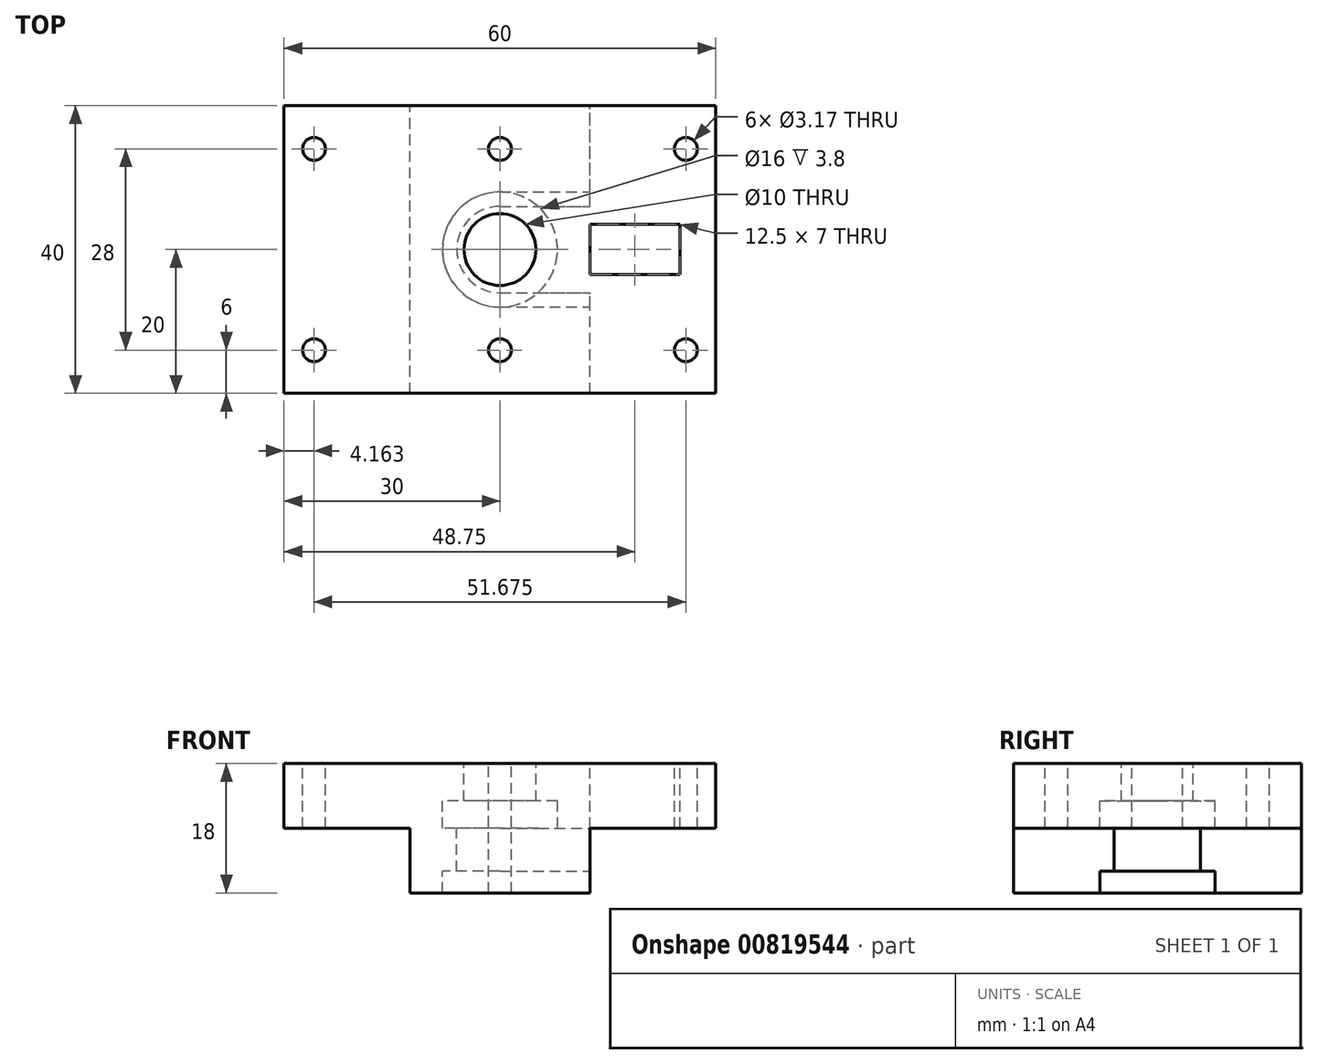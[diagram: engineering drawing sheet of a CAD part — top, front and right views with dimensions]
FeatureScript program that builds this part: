
annotation { "Feature Type Name" : "Feature", "Feature Type Description" : "" }
export const myFeature = defineFeature(function(context is Context, id is Id, definition is map)
    precondition{}
    {
        {
            var Q0;
            Q0=qCreatedBy(makeId("Top.planeOp"),FACE);
            var sketch = newSketch(context, id + "F0", { "sketchPlane" : qUnion([Q0])});
            skLineSegment(sketch, "E0.bottom", {"start": v(30, 20) * mm, "end": v(-30, 20) * mm});
            skLineSegment(sketch, "E0.top", {"start": v(30, -20) * mm, "end": v(-30, -20) * mm});
            skLineSegment(sketch, "E0.left", {"start": v(30, 20) * mm, "end": v(30, -20) * mm});
            skLineSegment(sketch, "E0.right", {"start": v(-30, 20) * mm, "end": v(-30, -20) * mm});
            skPoint(sketch, "E0.middle", {"position": v(0, 0) * mm});
            skLineSegment(sketch, "E1", {"start": v(-30, -20) * mm, "end": v(-30, -43.75) * mm});
            skLineSegment(sketch, "E2", {"start": v(30, -43.75) * mm, "end": v(30, -20) * mm});
            skLineSegment(sketch, "E3.bottom", {"start": v(24.25, -38.25) * mm, "end": v(-24.25, -38.25) * mm});
            skLineSegment(sketch, "E3.top", {"start": v(24.25, -21.75) * mm, "end": v(-24.25, -21.75) * mm});
            skLineSegment(sketch, "E3.left", {"start": v(24.25, -38.25) * mm, "end": v(24.25, -21.75) * mm});
            skLineSegment(sketch, "E3.right", {"start": v(-24.25, -38.25) * mm, "end": v(-24.25, -21.75) * mm});
            skPoint(sketch, "E3.middle", {"position": v(0, -30) * mm});
            skLineSegment(sketch, "E4", {"start": v(-24.25, -21.75) * mm, "end": v(-24.25, -20) * mm});
            skLineSegment(sketch, "E5", {"start": v(24.25, -21.75) * mm, "end": v(24.25, -20) * mm});
            skCircle(sketch, "E6", {"center": v(0, 0) * mm, "radius": 8 * mm});
            skCircle(sketch, "E7", {"center": v(0, -50) * mm, "radius": 6 * mm});
            skArc(sketch, "E8", {"start": v(-8.8, -60.89) * mm, "mid": v(0, -64) * mm, "end": v(8.8, -60.89) * mm});
            skLineSegment(sketch, "E9", {"start": v(-30, -43.75) * mm, "end": v(-8.8, -60.89) * mm});
            skLineSegment(sketch, "E10.MirrorCS", {"start": v(30, -43.75) * mm, "end": v(8.8, -60.89) * mm});
            skPoint(sketch, "E11.orphan", {"position": v(30, -62.25) * mm});
            skPoint(sketch, "E12.orphan", {"position": v(-30, -62.25) * mm});
            skCircle(sketch, "E13.MirrorC", {"center": v(-14, -50) * mm, "radius": 1.65 * mm});
            skCircle(sketch, "E14", {"center": v(0, 0) * mm, "radius": 5 * mm});
            skCircle(sketch, "E15", {"center": v(-25.84, 14) * mm, "radius": 1.59 * mm});
            skCircle(sketch, "E16.MirrorC", {"center": v(25.84, 14) * mm, "radius": 1.59 * mm});
            skCircle(sketch, "E17.MirrorC", {"center": v(25.84, -14) * mm, "radius": 1.59 * mm});
            skCircle(sketch, "E18.MirrorC", {"center": v(-25.84, -14) * mm, "radius": 1.59 * mm});
            skCircle(sketch, "E19.MirrorC", {"center": v(14, -50) * mm, "radius": 1.65 * mm});
            skCircle(sketch, "E20", {"center": v(14, -50) * mm, "radius": 3.85 * mm});
            skCircle(sketch, "E21.MirrorC", {"center": v(-14, -50) * mm, "radius": 3.85 * mm});
            skLineSegment(sketch, "E22.bottom", {"start": v(25, -3.5) * mm, "end": v(12.5, -3.5) * mm});
            skLineSegment(sketch, "E22.top", {"start": v(25, 3.5) * mm, "end": v(12.5, 3.5) * mm});
            skLineSegment(sketch, "E22.left", {"start": v(25, -3.5) * mm, "end": v(25, 3.5) * mm});
            skLineSegment(sketch, "E22.right", {"start": v(12.5, -3.5) * mm, "end": v(12.5, 3.5) * mm});
            skPoint(sketch, "E22.middle", {"position": v(18.75, 0) * mm});
            skCircle(sketch, "E23", {"center": v(0, 14) * mm, "radius": 1.59 * mm});
            skCircle(sketch, "E24.MirrorC", {"center": v(0, -14) * mm, "radius": 1.59 * mm});
            skSolve(sketch);
        }
        {
            var Q0;
            Q0=makeQuery(id+"F0.imprint","IMPRINT",FACE,{"disambiguationData":[TD([[makeQuery(id+"F0.imprint","IMPRINT",EDGE,{"derivedFrom":sQuery(id+"F0.wireOp",EDGE,"E0.bottom")}),1.0]])]});
            extrude(context, id + "F1", {"entities" : qUnion([Q0]), "oppositeDirection" : true, "depth" : 9 * mm, "offsetDistance" : 25 * mm});
        }
        {
            var Q0;
            Q0=makeQuery(id+"F0.imprint","IMPRINT",FACE,{"disambiguationData":[TD([[makeQuery(id+"F0.imprint","IMPRINT",EDGE,{"derivedFrom":sQuery(id+"F0.wireOp",EDGE,"E6")}),1.0]])]});
            var Q1;
            Q1=makeQuery(id+"F1.opExtrude","CAP_FACE",FACE,{"disambiguationData":[OSD([sQuery(id+"F0.wireOp",EDGE,"E0.bottom"),sQuery(id+"F0.wireOp",EDGE,"E0.top"),sQuery(id+"F0.wireOp",EDGE,"E0.left"),sQuery(id+"F0.wireOp",EDGE,"E0.right"),sQuery(id+"F0.wireOp",EDGE,"E1"),sQuery(id+"F0.wireOp",EDGE,"E2"),sQuery(id+"F0.wireOp",EDGE,"E3.bottom"),sQuery(id+"F0.wireOp",EDGE,"E3.left"),sQuery(id+"F0.wireOp",EDGE,"E3.right"),sQuery(id+"F0.wireOp",EDGE,"E4"),sQuery(id+"F0.wireOp",EDGE,"E5"),sQuery(id+"F0.wireOp",EDGE,"E6"),sQuery(id+"F0.wireOp",EDGE,"E7"),sQuery(id+"F0.wireOp",EDGE,"E8"),sQuery(id+"F0.wireOp",EDGE,"E9"),sQuery(id+"F0.wireOp",EDGE,"E10.MirrorCS"),sQuery(id+"F0.wireOp",EDGE,"E13.MirrorC"),sQuery(id+"F0.wireOp",EDGE,"E15"),sQuery(id+"F0.wireOp",EDGE,"E16.MirrorC"),sQuery(id+"F0.wireOp",EDGE,"E17.MirrorC"),sQuery(id+"F0.wireOp",EDGE,"E18.MirrorC"),sQuery(id+"F0.wireOp",EDGE,"E19.MirrorC")])],"isStart":false});
            extrude(context, id + "F2", {"entities" : qUnion([Q0]), "operationType" : NewBodyOperationType.ADD, "endBound" : BoundingType.UP_TO_SURFACE, "oppositeDirection" : true, "depth" : 2.2 * mm, "endBoundEntityFace" : qUnion([Q1]), "hasOffset" : true, "offsetDistance" : 3.8 * mm});
        }
        {
            var Q0;
            Q0=makeQuery(id+"F1.opExtrude","CAP_FACE",FACE,{"disambiguationData":[OSD([sQuery(id+"F0.wireOp",EDGE,"E0.bottom"),sQuery(id+"F0.wireOp",EDGE,"E0.top"),sQuery(id+"F0.wireOp",EDGE,"E0.left"),sQuery(id+"F0.wireOp",EDGE,"E0.right"),sQuery(id+"F0.wireOp",EDGE,"E1"),sQuery(id+"F0.wireOp",EDGE,"E2"),sQuery(id+"F0.wireOp",EDGE,"E3.bottom"),sQuery(id+"F0.wireOp",EDGE,"E3.left"),sQuery(id+"F0.wireOp",EDGE,"E3.right"),sQuery(id+"F0.wireOp",EDGE,"E4"),sQuery(id+"F0.wireOp",EDGE,"E5"),sQuery(id+"F0.wireOp",EDGE,"E6"),sQuery(id+"F0.wireOp",EDGE,"E7"),sQuery(id+"F0.wireOp",EDGE,"E8"),sQuery(id+"F0.wireOp",EDGE,"E9"),sQuery(id+"F0.wireOp",EDGE,"E10.MirrorCS"),sQuery(id+"F0.wireOp",EDGE,"E15"),sQuery(id+"F0.wireOp",EDGE,"E16.MirrorC"),sQuery(id+"F0.wireOp",EDGE,"E17.MirrorC"),sQuery(id+"F0.wireOp",EDGE,"E18.MirrorC"),sQuery(id+"F0.wireOp",EDGE,"E20"),sQuery(id+"F0.wireOp",EDGE,"E21.MirrorC"),sQuery(id+"F0.wireOp",EDGE,"E22.bottom"),sQuery(id+"F0.wireOp",EDGE,"E22.top"),sQuery(id+"F0.wireOp",EDGE,"E22.left"),sQuery(id+"F0.wireOp",EDGE,"E22.right")])],"isStart":false});
            var sketch = newSketch(context, id + "F3", { "sketchPlane" : qUnion([Q0])});
            skLineSegment(sketch, "E25.bottom", {"start": v(-12.5, 20) * mm, "end": v(12.5, 20) * mm});
            skLineSegment(sketch, "E25.top", {"start": v(-12.5, -20) * mm, "end": v(12.5, -20) * mm});
            skLineSegment(sketch, "E25.left", {"start": v(-12.5, 20) * mm, "end": v(-12.5, -20) * mm});
            skLineSegment(sketch, "E25.right", {"start": v(12.5, 20) * mm, "end": v(12.5, -20) * mm});
            skPoint(sketch, "E25.middle", {"position": v(0, 0) * mm});
            skArc(sketch, "E26", {"start": v(0, 6) * mm, "mid": v(-6, 0) * mm, "end": v(0, -6) * mm});
            skLineSegment(sketch, "E27", {"start": v(0, 8) * mm, "end": v(12.5, 8) * mm});
            skLineSegment(sketch, "E28.MirrorCS", {"start": v(0, -8) * mm, "end": v(12.5, -8) * mm});
            skLineSegment(sketch, "E29", {"start": v(0, 6) * mm, "end": v(12.5, 6) * mm});
            skLineSegment(sketch, "E30", {"start": v(0, -6) * mm, "end": v(12.5, -6) * mm});
            skArc(sketch, "E31", {"start": v(0, 8) * mm, "mid": v(-8, 0) * mm, "end": v(0, -8) * mm});
            skSolve(sketch);
        }
        {
            var Q0;
            {var subQ1=sQuery(id+"F3.wireOp",EDGE,"E25.bottom");Q0=makeQuery(id+"F3.imprint","IMPRINT",FACE,{"disambiguationData":[TD([[makeQuery(id+"F3.imprint","IMPRINT",EDGE,{"derivedFrom":subQ1}),1.0]])]});}
            extrude(context, id + "F4", {"entities" : qUnion([Q0]), "depth" : 9 * mm, "offsetDistance" : 25 * mm});
        }
        {
            var Q0;
            {var subQ0=sQuery(id+"F3.wireOp",EDGE,"E28.MirrorCS");Q0=makeQuery(id+"F3.imprint","IMPRINT",FACE,{"disambiguationData":[TD([[makeQuery(id+"F3.imprint","IMPRINT",EDGE,{"derivedFrom":subQ0}),1.0]])]});}
            var Q1;
            {var subQ4=sQuery(id+"F3.wireOp",EDGE,"E26");var subQ7=sQuery(id+"F3.wireOp",EDGE,"E29");var subQ8=makeQuery(id+"F3.imprint","INTERSECT",VERTEX,{"derivedFrom":[subQ4,subQ7]});Q1=makeQuery(id+"F3.imprint","IMPRINT",FACE,{"disambiguationData":[TD([[makeQuery(id+"F3.imprint","IMPRINT",EDGE,{"disambiguationData":[TD([[subQ8,-1.0]])],"derivedFrom":subQ4}),-1.0]])]});}
            var Q2;
            {var subQ0=sQuery(id+"F3.wireOp",EDGE,"E27");Q2=makeQuery(id+"F3.imprint","IMPRINT",FACE,{"disambiguationData":[TD([[makeQuery(id+"F3.imprint","IMPRINT",EDGE,{"derivedFrom":subQ0}),-1.0]])]});}
            extrude(context, id + "F5", {"entities" : qUnion([Q0, Q1, Q2]), "operationType" : NewBodyOperationType.ADD, "depth" : 6 * mm, "offsetDistance" : 25 * mm});
        }
        {
            var Q0;
            Q0=qCreatedBy(makeId("Right.planeOp"),FACE);
            var sketch = newSketch(context, id + "F6", { "sketchPlane" : qUnion([Q0])});
            skPoint(sketch, "E32", {"position": v(-30, -16.6) * mm});
            skCircle(sketch, "E33", {"center": v(-30, -16.6) * mm, "radius": 5 * mm});
            skSolve(sketch);
        }
    });
